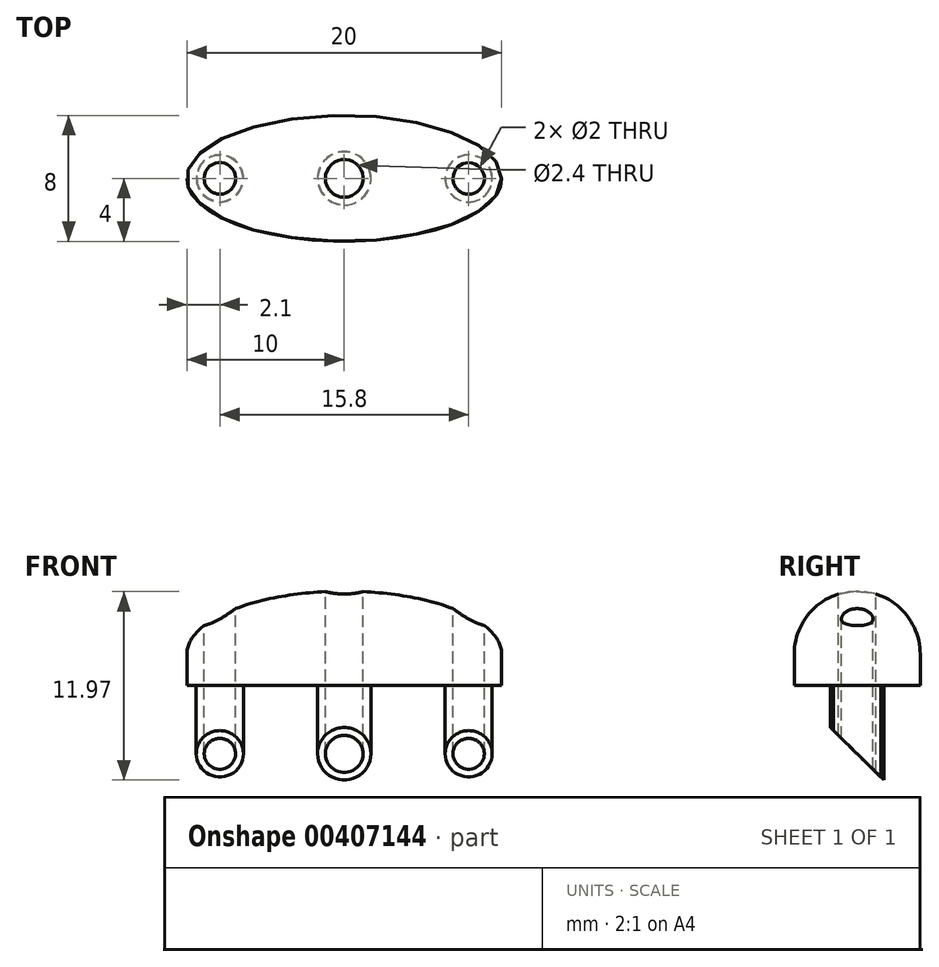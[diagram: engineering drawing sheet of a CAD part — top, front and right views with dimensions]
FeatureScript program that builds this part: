
annotation { "Feature Type Name" : "Feature", "Feature Type Description" : "" }
export const myFeature = defineFeature(function(context is Context, id is Id, definition is map)
    precondition{}
    {
        {
            var Q0;
            Q0=qCreatedBy(makeId("Top.planeOp"),FACE);
            var sketch = newSketch(context, id + "F0", { "sketchPlane" : qUnion([Q0])});
            skLineSegment(sketch, "E0", {"start": v(-10, 0) * mm, "end": v(10, 0) * mm, "construction": true});
            skLineSegment(sketch, "E1", {"start": v(0, -4) * mm, "end": v(0, 4) * mm, "construction": true});
            skEllipse(sketch, "E2", {"center": v(0, 0) * mm, "majorRadius": 10 * mm, "minorRadius": 4 * mm, "majorAxis": v(1, 0)});
            skSolve(sketch);
        }
        {
            var Q0;
            Q0 = qSketchRegion(id + "F0", true);
            extrude(context, id + "F1", {"entities" : qUnion([Q0]), "depth" : 2 * mm, "offsetDistance" : 25 * mm});
        }
        {
            var Q0;
            Q0=makeQuery(id+"F1.opExtrude","CAP_FACE",FACE,{"disambiguationData":[OSD([sQuery(id+"F0.wireOp",EDGE,"E2")])],"isStart":true});
            var sketch = newSketch(context, id + "F2", { "sketchPlane" : qUnion([Q0])});
            skLineSegment(sketch, "E3", {"start": v(-10, 0) * mm, "end": v(10, 0) * mm, "construction": true});
            skLineSegment(sketch, "E4", {"start": v(0, -4) * mm, "end": v(0, 4) * mm, "construction": true});
            skCircle(sketch, "E5", {"center": v(-7.9, 0) * mm, "radius": 1.5 * mm});
            skCircle(sketch, "E6", {"center": v(7.9, 0) * mm, "radius": 1.5 * mm});
            skCircle(sketch, "E7", {"center": v(-7.9, 0) * mm, "radius": 1 * mm});
            skCircle(sketch, "E8", {"center": v(7.9, 0) * mm, "radius": 1 * mm});
            skCircle(sketch, "E9", {"center": v(0, 0) * mm, "radius": 1.7 * mm});
            skCircle(sketch, "E10", {"center": v(0, 0) * mm, "radius": 1.2 * mm});
            skSolve(sketch);
        }
        {
            var Q0;
            Q0 = qSketchRegion(id + "F2", true);
            extrude(context, id + "F3", {"entities" : qUnion([Q0]), "operationType" : NewBodyOperationType.ADD, "depth" : 6 * mm, "offsetDistance" : 25 * mm});
        }
        {
            var Q0;
            Q0=makeQuery(id+"F1.opExtrude","CAP_FACE",FACE,{"disambiguationData":[OSD([sQuery(id+"F0.wireOp",EDGE,"E2")])],"isStart":false});
            var sketch = newSketch(context, id + "F4", { "sketchPlane" : qUnion([Q0])});
            skEllipticalArc(sketch, "E11.0", {});
            skLineSegment(sketch, "E12", {"start": v(-10, 0) * mm, "end": v(10, 0) * mm, "construction": true});
            skLineSegment(sketch, "E13", {"start": v(-10, 0) * mm, "end": v(10, 0) * mm});
            const initialGuessF4  = {"E11.0": [0, 0, 1, 0, 0.01, 0.004, 0, 3.141592653589793]};
            skSetInitialGuess(sketch, initialGuessF4);
            skSolve(sketch);
        }
        {
            var Q0;
            Q0 = qSketchRegion(id + "F4", true);
            var Q1;
            Q1=sQuery(id+"F4.wireOp",EDGE,"E12");
            revolve(context, id + "F5", {"operationType" : NewBodyOperationType.ADD, "entities" : qUnion([Q0]), "axis" : qUnion([Q1]), "revolveType" : RevolveType.ONE_DIRECTION, "angle" : 180 * degree});
        }
        {
            var Q0;
            {var subQ0=sQuery(id+"F0.wireOp",EDGE,"E2");Q0=makeQuery(id+"F3.boolean.opBoolean","SPLIT",FACE,{"disambiguationData":[TD([makeQuery(id+"F1.opExtrude","SWEPT_FACE",FACE,{"disambiguationData":[OSD([subQ0])]})])],"derivedFrom":makeQuery(id+"F1.opExtrude","CAP_FACE",FACE,{"disambiguationData":[OSD([subQ0])],"isStart":true})});}
            var sketch = newSketch(context, id + "F6", { "sketchPlane" : qUnion([Q0])});
            skCircle(sketch, "E14.0", {"center": v(-7.9, 0) * mm, "radius": 1 * mm});
            skCircle(sketch, "E15.0", {"center": v(0, 0) * mm, "radius": 1.2 * mm});
            skCircle(sketch, "E16.0", {"center": v(7.9, 0) * mm, "radius": 1 * mm});
            skSolve(sketch);
        }
        {
            var Q0;
            Q0 = qSketchRegion(id + "F6", true);
            extrude(context, id + "F7", {"entities" : qUnion([Q0]), "operationType" : NewBodyOperationType.REMOVE, "endBound" : BoundingType.THROUGH_ALL, "oppositeDirection" : true, "depth" : 25 * mm, "offsetDistance" : 25 * mm});
        }
        {
            var Q0;
            Q0=qCreatedBy(makeId("Right.planeOp"),FACE);
            var sketch = newSketch(context, id + "F8", { "sketchPlane" : qUnion([Q0])});
            skLineSegment(sketch, "E17.0", {"start": v(1.7, -6) * mm, "end": v(-1.7, -6) * mm});
            skLineSegment(sketch, "E18", {"start": v(1.7, -6) * mm, "end": v(-1.7, -2.66) * mm});
            skLineSegment(sketch, "E19", {"start": v(-1.7, -6) * mm, "end": v(-1.7, -2.66) * mm});
            skSolve(sketch);
        }
        {
            var Q0;
            Q0 = qSketchRegion(id + "F8", true);
            extrude(context, id + "F9", {"entities" : qUnion([Q0]), "operationType" : NewBodyOperationType.REMOVE, "endBound" : BoundingType.SYMMETRIC, "oppositeDirection" : true, "depth" : 25 * mm, "offsetDistance" : 25 * mm});
        }
    });
